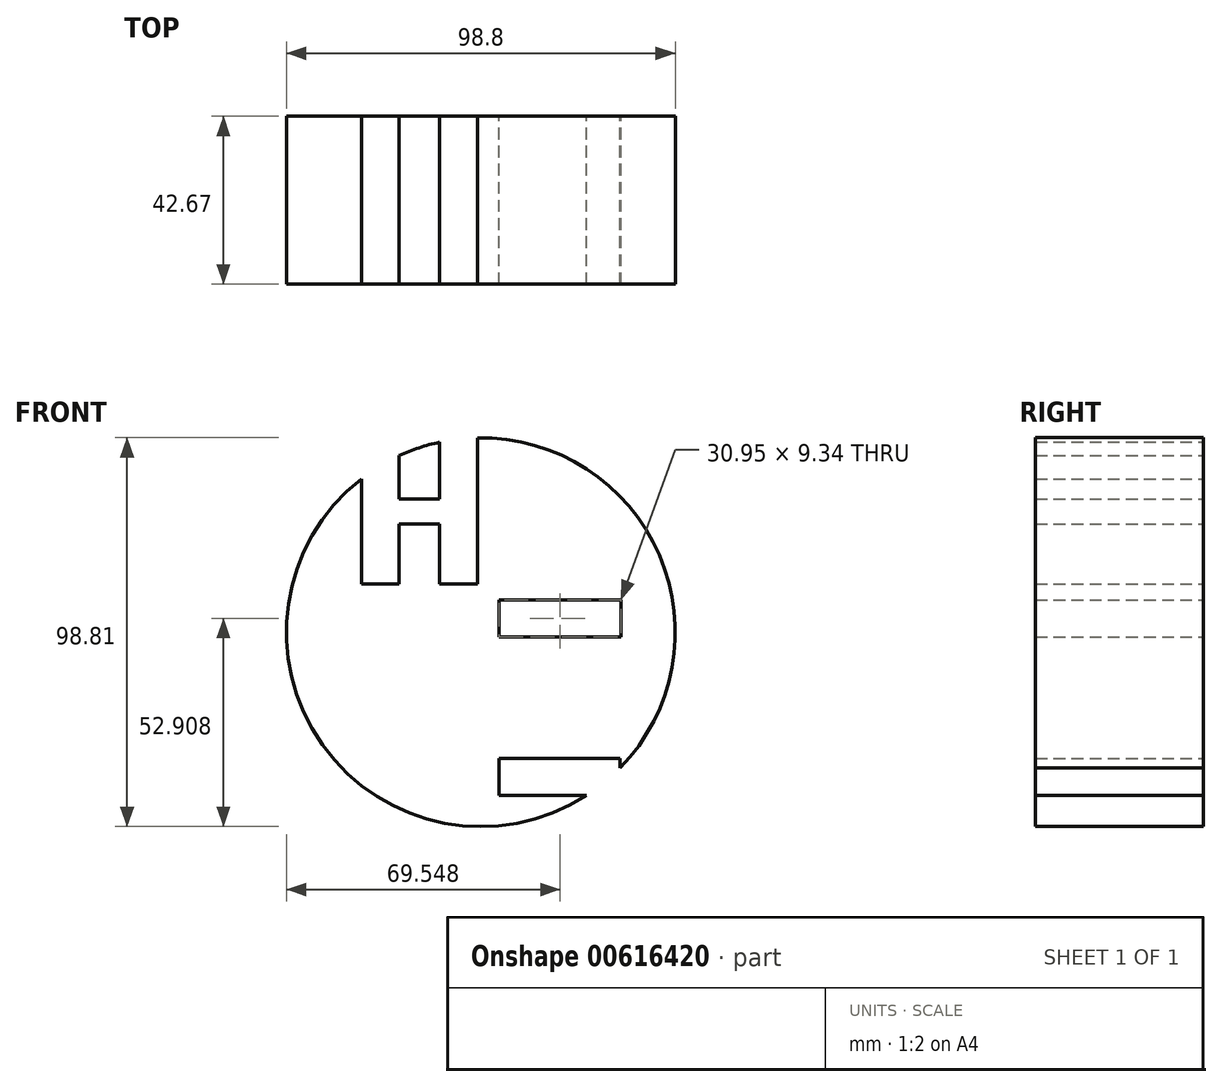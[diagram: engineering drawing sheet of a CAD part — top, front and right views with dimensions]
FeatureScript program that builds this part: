
annotation { "Feature Type Name" : "Feature", "Feature Type Description" : "" }
export const myFeature = defineFeature(function(context is Context, id is Id, definition is map)
    precondition{}
    {
        {
            var Q0;
            Q0=qCreatedBy(makeId("Front.planeOp"),FACE);
            var sketch = newSketch(context, id + "F0", { "sketchPlane" : qUnion([Q0])});
            skCircle(sketch, "E0", {"center": v(-16.8, 8.61) * mm, "radius": 49.4 * mm});
            skSolve(sketch);
        }
        {
            var Q0;
            Q0=makeQuery(id+"F0.imprint","IMPRINT",FACE,{"disambiguationData":[TD([[makeQuery(id+"F0.imprint","IMPRINT",EDGE,{"derivedFrom":sQuery(id+"F0.wireOp",EDGE,"E0")}),1.0]])]});
            extrude(context, id + "F1", {"entities" : qUnion([Q0]), "depth" : 42.67 * mm, "offsetDistance" : 25.4 * mm});
        }
        {
            var Q0;
            Q0=qCreatedBy(makeId("Front.planeOp"),FACE);
            var sketch = newSketch(context, id + "F2", { "sketchPlane" : qUnion([Q0])});
            skLineSegment(sketch, "E1.bottom", {"start": v(-47.16, 57.67) * mm, "end": v(-37.52, 57.67) * mm});
            skLineSegment(sketch, "E1.top", {"start": v(-47.16, 20.88) * mm, "end": v(-37.52, 20.88) * mm});
            skLineSegment(sketch, "E1.left", {"start": v(-47.16, 57.67) * mm, "end": v(-47.16, 20.88) * mm});
            skLineSegment(sketch, "E1.right", {"start": v(-37.52, 57.67) * mm, "end": v(-37.52, 20.88) * mm});
            skLineSegment(sketch, "E2.bottom", {"start": v(-37.52, 42.49) * mm, "end": v(-27.3, 42.49) * mm});
            skLineSegment(sketch, "E2.top", {"start": v(-37.52, 36.06) * mm, "end": v(-27.3, 36.06) * mm});
            skLineSegment(sketch, "E2.left", {"start": v(-37.52, 42.49) * mm, "end": v(-37.52, 36.06) * mm});
            skLineSegment(sketch, "E2.right", {"start": v(-27.3, 42.49) * mm, "end": v(-27.3, 36.06) * mm});
            skLineSegment(sketch, "E3.bottom", {"start": v(-27.3, 58.84) * mm, "end": v(-17.67, 58.84) * mm});
            skLineSegment(sketch, "E3.top", {"start": v(-27.3, 20.88) * mm, "end": v(-17.67, 20.88) * mm});
            skLineSegment(sketch, "E3.left", {"start": v(-27.3, 58.84) * mm, "end": v(-27.3, 20.88) * mm});
            skLineSegment(sketch, "E3.right", {"start": v(-17.67, 58.84) * mm, "end": v(-17.67, 20.88) * mm});
            skLineSegment(sketch, "E4.bottom", {"start": v(-12.12, -23.5) * mm, "end": v(18.54, -23.5) * mm});
            skLineSegment(sketch, "E4.top", {"start": v(-12.12, -32.85) * mm, "end": v(18.54, -32.85) * mm});
            skLineSegment(sketch, "E4.left", {"start": v(-12.12, -23.5) * mm, "end": v(-12.12, -32.85) * mm});
            skLineSegment(sketch, "E4.right", {"start": v(18.54, -23.5) * mm, "end": v(18.54, -32.85) * mm});
            skPoint(sketch, "E5.firstSnap0", {"position": v(3.21, -23.5) * mm});
            skLineSegment(sketch, "E5.bottom", {"start": v(0, -23.5) * mm, "end": v(8.61, -23.5) * mm});
            skLineSegment(sketch, "E5.top", {"start": v(0, 7.45) * mm, "end": v(8.61, 7.45) * mm});
            skLineSegment(sketch, "E5.left", {"start": v(0, -23.5) * mm, "end": v(0, 7.45) * mm});
            skLineSegment(sketch, "E5.right", {"start": v(8.61, -23.5) * mm, "end": v(8.61, 7.45) * mm});
            skLineSegment(sketch, "E6.bottom", {"start": v(-12.12, 7.45) * mm, "end": v(18.83, 7.45) * mm});
            skLineSegment(sketch, "E6.top", {"start": v(-12.12, 16.8) * mm, "end": v(18.83, 16.8) * mm});
            skLineSegment(sketch, "E6.left", {"start": v(-12.12, 7.45) * mm, "end": v(-12.12, 16.8) * mm});
            skLineSegment(sketch, "E6.right", {"start": v(18.83, 7.45) * mm, "end": v(18.83, 16.8) * mm});
            skSolve(sketch);
        }
        {
            var Q0;
            Q0=makeQuery(id+"F2.imprint","IMPRINT",FACE,{"disambiguationData":[TD([[makeQuery(id+"F2.imprint","IMPRINT",EDGE,{"derivedFrom":sQuery(id+"F2.wireOp",EDGE,"E5.bottom")}),1.0]])]});
            var Q1;
            {var subQ0=sQuery(id+"F2.wireOp",EDGE,"E2.bottom");Q1=makeQuery(id+"F2.imprint","IMPRINT",FACE,{"disambiguationData":[TD([[makeQuery(id+"F2.imprint","IMPRINT",EDGE,{"derivedFrom":subQ0}),-1.0]])]});}
            var Q2;
            Q2=makeQuery(id+"F2.imprint","IMPRINT",FACE,{"disambiguationData":[TD([[makeQuery(id+"F2.imprint","IMPRINT",EDGE,{"derivedFrom":sQuery(id+"F2.wireOp",EDGE,"E6.top")}),-1.0]])]});
            var Q3;
            Q3=makeQuery(id+"F2.imprint","IMPRINT",FACE,{"disambiguationData":[TD([[makeQuery(id+"F2.imprint","IMPRINT",EDGE,{"derivedFrom":sQuery(id+"F2.wireOp",EDGE,"E4.top")}),1.0]])]});
            var Q4;
            {var subQ3=sQuery(id+"F2.wireOp",EDGE,"E3.bottom");Q4=makeQuery(id+"F2.imprint","IMPRINT",FACE,{"disambiguationData":[TD([[makeQuery(id+"F2.imprint","IMPRINT",EDGE,{"derivedFrom":subQ3}),-1.0]])]});}
            var Q5;
            {var subQ1=sQuery(id+"F2.wireOp",EDGE,"E1.bottom");Q5=makeQuery(id+"F2.imprint","IMPRINT",FACE,{"disambiguationData":[TD([[makeQuery(id+"F2.imprint","IMPRINT",EDGE,{"derivedFrom":subQ1}),-1.0]])]});}
            extrude(context, id + "F3", {"entities" : qUnion([Q0, Q1, Q2, Q3, Q4, Q5]), "operationType" : NewBodyOperationType.REMOVE, "depth" : 57.4 * mm, "offsetDistance" : 25.4 * mm});
        }
    });
